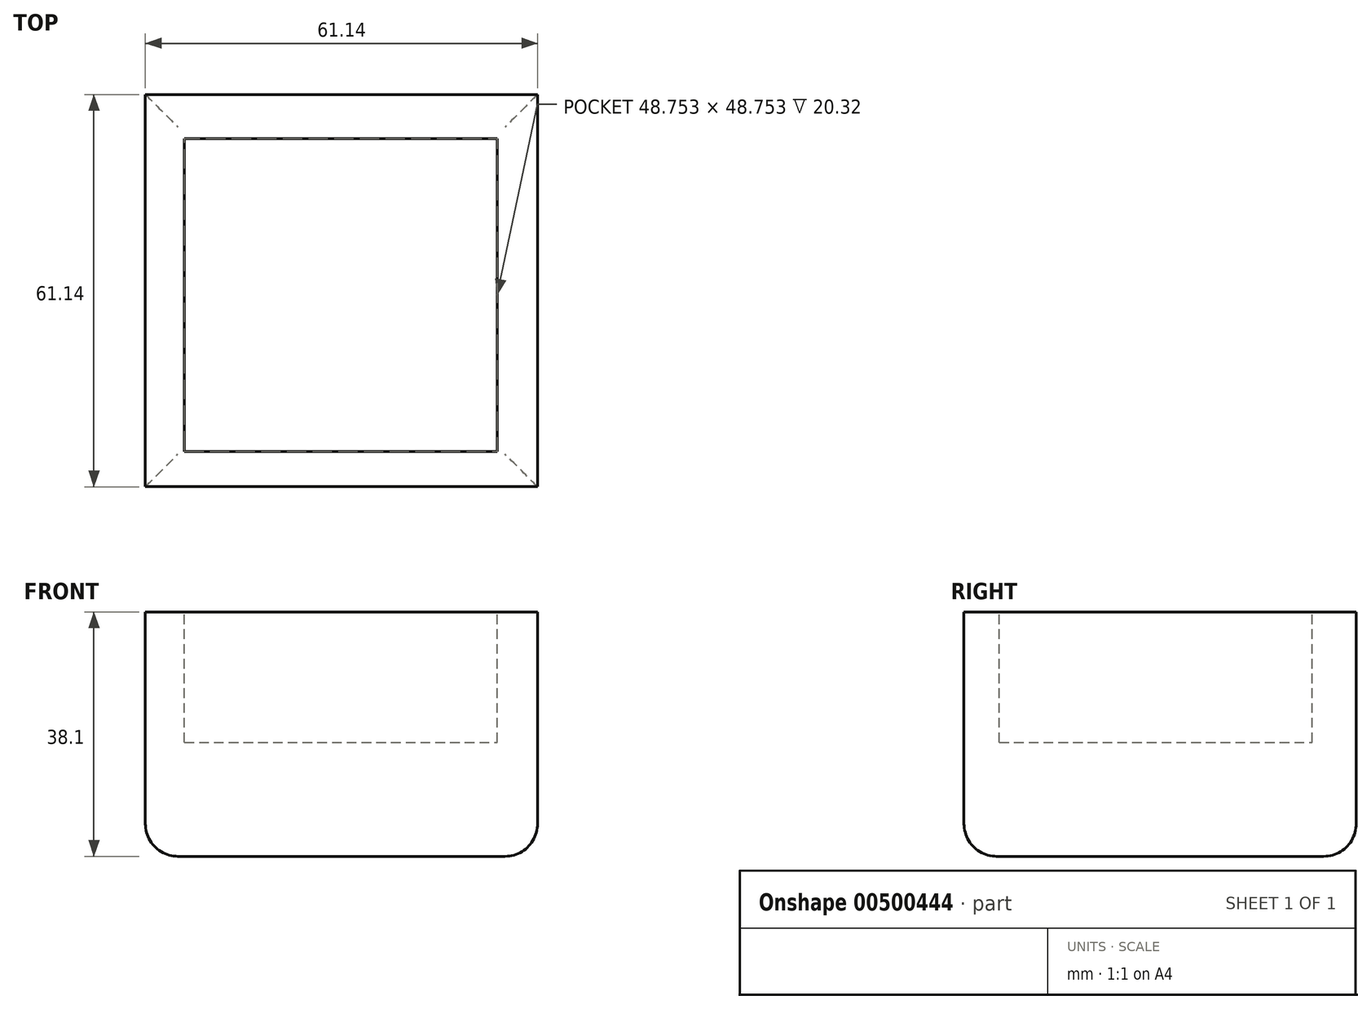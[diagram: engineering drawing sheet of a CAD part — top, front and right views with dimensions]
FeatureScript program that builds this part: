
annotation { "Feature Type Name" : "Feature", "Feature Type Description" : "" }
export const myFeature = defineFeature(function(context is Context, id is Id, definition is map)
    precondition{}
    {
        {
            var Q0;
            Q0=qCreatedBy(makeId("Top.planeOp"),FACE);
            var sketch = newSketch(context, id + "F0", { "sketchPlane" : qUnion([Q0])});
            skLineSegment(sketch, "E0.bottom", {"start": v(-41.68, -11.8) * mm, "end": v(19.46, -11.8) * mm});
            skLineSegment(sketch, "E0.top", {"start": v(-41.68, 49.34) * mm, "end": v(19.46, 49.34) * mm});
            skLineSegment(sketch, "E0.left", {"start": v(-41.68, -11.8) * mm, "end": v(-41.68, 49.34) * mm});
            skLineSegment(sketch, "E0.right", {"start": v(19.46, -11.8) * mm, "end": v(19.46, 49.34) * mm});
            skSolve(sketch);
        }
        {
            var Q0;
            Q0=makeQuery(id+"F0.imprint","IMPRINT",FACE,{"disambiguationData":[TD([[makeQuery(id+"F0.imprint","IMPRINT",EDGE,{"derivedFrom":sQuery(id+"F0.wireOp",EDGE,"E0.bottom")}),1.0]])]});
            extrude(context, id + "F1", {"entities" : qUnion([Q0]), "depth" : 38.1 * mm, "offsetDistance" : 25.4 * mm});
        }
        {
            var Q0;
            Q0=makeQuery(id+"F1.opExtrude","CAP_FACE",FACE,{"disambiguationData":[OSD([sQuery(id+"F0.wireOp",EDGE,"E0.bottom"),sQuery(id+"F0.wireOp",EDGE,"E0.top"),sQuery(id+"F0.wireOp",EDGE,"E0.left"),sQuery(id+"F0.wireOp",EDGE,"E0.right")])],"isStart":false});
            var sketch = newSketch(context, id + "F2", { "sketchPlane" : qUnion([Q0])});
            skLineSegment(sketch, "E1.bottom", {"start": v(-35.58, -6.3) * mm, "end": v(13.17, -6.3) * mm});
            skLineSegment(sketch, "E1.top", {"start": v(-35.58, 42.46) * mm, "end": v(13.17, 42.46) * mm});
            skLineSegment(sketch, "E1.left", {"start": v(-35.58, -6.3) * mm, "end": v(-35.58, 42.46) * mm});
            skLineSegment(sketch, "E1.right", {"start": v(13.17, -6.3) * mm, "end": v(13.17, 42.46) * mm});
            skSolve(sketch);
        }
        {
            var Q0;
            Q0=makeQuery(id+"F2.imprint","IMPRINT",FACE,{"disambiguationData":[TD([[makeQuery(id+"F2.imprint","IMPRINT",EDGE,{"derivedFrom":sQuery(id+"F2.wireOp",EDGE,"E1.bottom")}),1.0]])]});
            extrude(context, id + "F3", {"entities" : qUnion([Q0]), "operationType" : NewBodyOperationType.REMOVE, "oppositeDirection" : true, "depth" : 20.32 * mm, "offsetDistance" : 25.4 * mm});
        }
        {
            var Q0;
            Q0=makeQuery(id+"F3.boolean.opBoolean","COPY",EDGE,{"derivedFrom":makeQuery(id+"F3.opExtrude","CAP_EDGE",EDGE,{"disambiguationData":[OSD([sQuery(id+"F2.wireOp",EDGE,"E1.top")])],"isStart":true})});
            var Q1;
            Q1=makeQuery(id+"F3.boolean.opBoolean","COPY",EDGE,{"derivedFrom":makeQuery(id+"F3.opExtrude","CAP_EDGE",EDGE,{"disambiguationData":[OSD([sQuery(id+"F2.wireOp",EDGE,"E1.left")])],"isStart":true})});
            var Q2;
            Q2=makeQuery(id+"F3.boolean.opBoolean","COPY",EDGE,{"derivedFrom":makeQuery(id+"F3.opExtrude","CAP_EDGE",EDGE,{"disambiguationData":[OSD([sQuery(id+"F2.wireOp",EDGE,"E1.right")])],"isStart":true})});
            var Q3;
            Q3=makeQuery(id+"F3.boolean.opBoolean","COPY",EDGE,{"derivedFrom":makeQuery(id+"F3.opExtrude","CAP_EDGE",EDGE,{"disambiguationData":[OSD([sQuery(id+"F2.wireOp",EDGE,"E1.bottom")])],"isStart":true})});
            var Q4;
            Q4=makeQuery(id+"F1.opExtrude","CAP_EDGE",EDGE,{"disambiguationData":[OSD([sQuery(id+"F0.wireOp",EDGE,"E0.right")])],"isStart":true});
            var Q5;
            Q5=makeQuery(id+"F1.opExtrude","CAP_EDGE",EDGE,{"disambiguationData":[OSD([sQuery(id+"F0.wireOp",EDGE,"E0.bottom")])],"isStart":true});
            var Q6;
            Q6=makeQuery(id+"F1.opExtrude","CAP_EDGE",EDGE,{"disambiguationData":[OSD([sQuery(id+"F0.wireOp",EDGE,"E0.left")])],"isStart":true});
            var Q7;
            Q7=makeQuery(id+"F1.opExtrude","CAP_EDGE",EDGE,{"disambiguationData":[OSD([sQuery(id+"F0.wireOp",EDGE,"E0.top")])],"isStart":true});
            fillet(context, id + "F4", {"entities" : qUnion([Q0, Q1, Q2, Q3, Q4, Q5, Q6, Q7]), "radius" : 5.08 * mm, "tangentPropagation" : true, "allowEdgeOverflow" : false});
        }
    });
